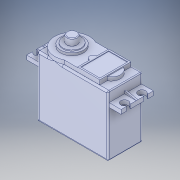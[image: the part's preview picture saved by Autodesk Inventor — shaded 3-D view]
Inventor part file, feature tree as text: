
AUTODESK INVENTOR PART (.ipt)
format: ipt  version: 2019 (Build 230136000, 136)  size: 333,312 bytes
history: mixed  units: mm
features: fillet x1, imported_body x1
ambient origin geometry x8: Origin, YZ Plane, XZ Plane, XY Plane, X Axis, Y Axis, Z Axis, Center Point
bodies: Solid1 (imported_parasolid)
feature tree (2):
  fillet  "Redondeo5"  [1 undecoded]
  imported_body  NMx_Import_Brep_tag  [imported B-rep: ~6 faces, bbox_mm=None]
note: 1 required parameter value undecoded (feature->parameter linkage not recoverable at this tier; creation-order binding heuristic only, values carry confidence <= 0.55)
